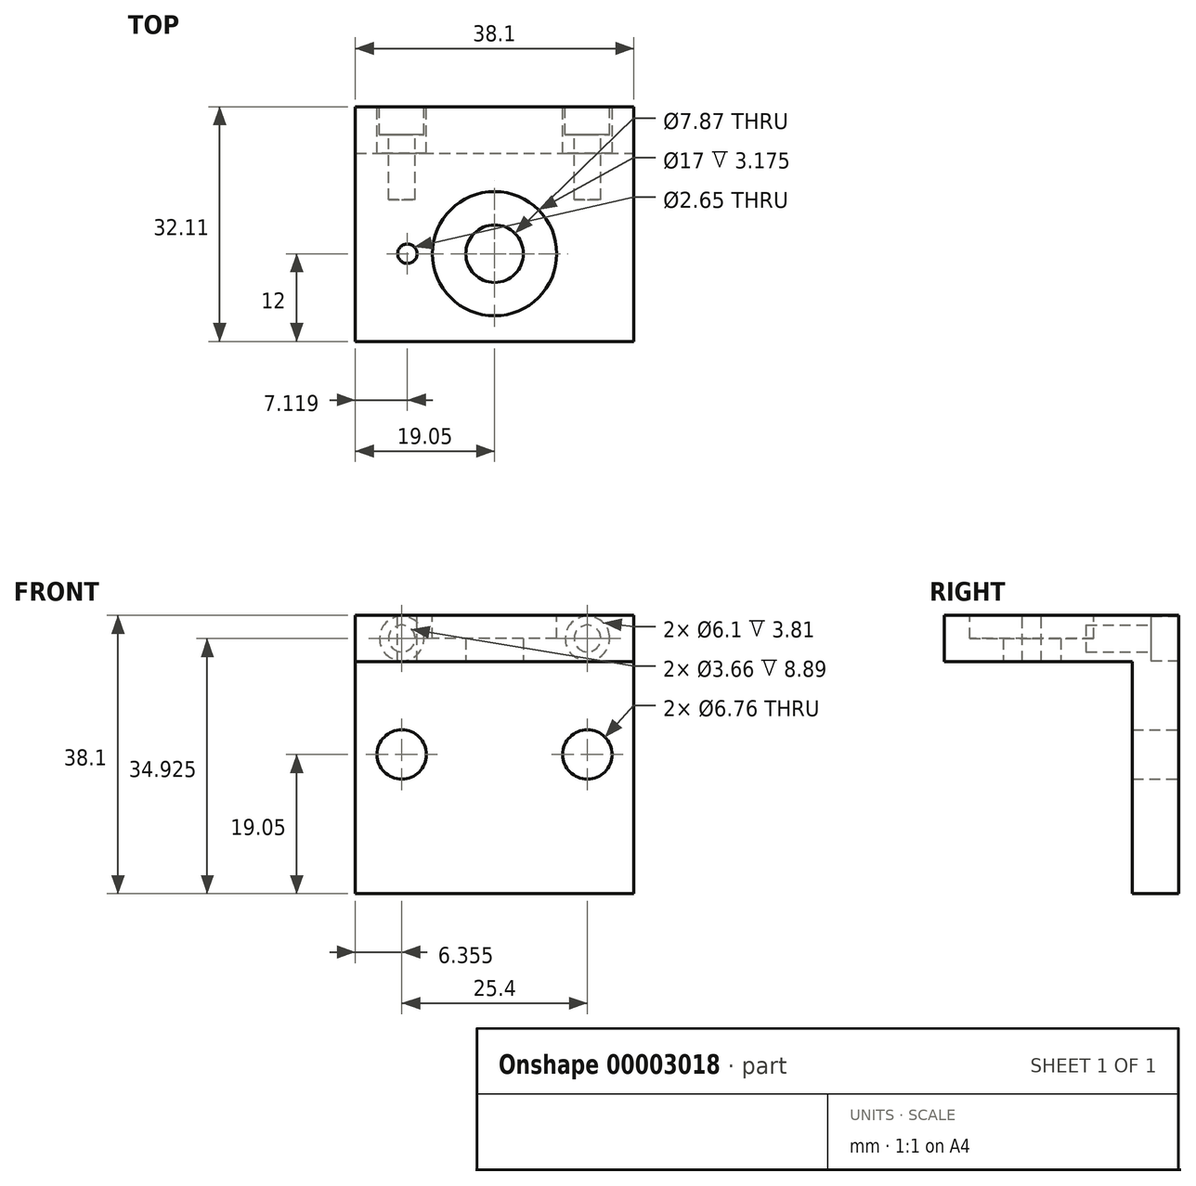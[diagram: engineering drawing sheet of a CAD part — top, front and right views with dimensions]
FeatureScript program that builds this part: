
annotation { "Feature Type Name" : "Feature", "Feature Type Description" : "" }
export const myFeature = defineFeature(function(context is Context, id is Id, definition is map)
    precondition{}
    {
        {
            var Q0;
            Q0=qCreatedBy(makeId("Top.planeOp"),FACE);
            var sketch = newSketch(context, id + "F0", { "sketchPlane" : qUnion([Q0])});
            skCircle(sketch, "E0", {"center": v(0, 0) * mm, "radius": 3.94 * mm});
            skArc(sketch, "E1", {"start": v(-11.93, 1.32) * mm, "mid": v(-12, 0) * mm, "end": v(-11.93, -1.33) * mm});
            skLineSegment(sketch, "E2", {"start": v(-10.8, 0.7) * mm, "end": v(-10.8, -0.7) * mm});
            skLineSegment(sketch, "E3", {"start": v(-11.93, 1.32) * mm, "end": v(-10.8, 0.7) * mm});
            skLineSegment(sketch, "E4.0.MirrorCS", {"start": v(-11.93, -1.32) * mm, "end": v(-10.8, -0.7) * mm});
            skCircle(sketch, "E5", {"center": v(0, 0) * mm, "radius": 12 * mm});
            skSolve(sketch);
        }
        {
            var Q0;
            Q0=makeQuery(id+"F0.imprint","IMPRINT",FACE,{"disambiguationData":[TD([[makeQuery(id+"F0.imprint","IMPRINT",EDGE,{"derivedFrom":sQuery(id+"F0.wireOp",EDGE,"E0")}),-1.0]])]});
            extrude(context, id + "F1", {"entities" : qUnion([Q0]), "depth" : 6.35 * mm});
        }
        {
            var Q0;
            Q0=makeQuery(id+"F1.opExtrude","CAP_FACE",FACE,{"disambiguationData":[OSD([sQuery(id+"F0.wireOp",EDGE,"E0"),sQuery(id+"F0.wireOp",EDGE,"E2"),sQuery(id+"F0.wireOp",EDGE,"E3"),sQuery(id+"F0.wireOp",EDGE,"E4.0.MirrorCS"),sQuery(id+"F0.wireOp",EDGE,"E5")])],"isStart":false});
            var sketch = newSketch(context, id + "F2", { "sketchPlane" : qUnion([Q0])});
            skCircle(sketch, "E6", {"center": v(0, 0) * mm, "radius": 8.5 * mm});
            skSolve(sketch);
        }
        {
            var Q0;
            Q0=makeQuery(id+"F2.imprint","IMPRINT",FACE,{"disambiguationData":[TD([[makeQuery(id+"F2.imprint","IMPRINT",EDGE,{"derivedFrom":sQuery(id+"F2.wireOp",EDGE,"E6")}),1.0]])]});
            extrude(context, id + "F3", {"entities" : qUnion([Q0]), "operationType" : NewBodyOperationType.REMOVE, "oppositeDirection" : true, "depth" : 3.17 * mm});
        }
        {
            var Q0;
            Q0=makeQuery(id+"F1.opExtrude","CAP_FACE",FACE,{"disambiguationData":[OSD([sQuery(id+"F0.wireOp",EDGE,"E0"),sQuery(id+"F0.wireOp",EDGE,"E2"),sQuery(id+"F0.wireOp",EDGE,"E3"),sQuery(id+"F0.wireOp",EDGE,"E4.0.MirrorCS"),sQuery(id+"F0.wireOp",EDGE,"E5")])],"isStart":false});
            var sketch = newSketch(context, id + "F4", { "sketchPlane" : qUnion([Q0])});
            skLineSegment(sketch, "E7.bottom", {"start": v(-11.93, 1.33) * mm, "end": v(11.94, 1.33) * mm});
            skLineSegment(sketch, "E7.top", {"start": v(-11.93, 13.76) * mm, "end": v(11.94, 13.76) * mm});
            skLineSegment(sketch, "E7.left", {"start": v(-11.93, 1.33) * mm, "end": v(-11.93, 13.76) * mm});
            skLineSegment(sketch, "E7.right", {"start": v(11.94, 1.33) * mm, "end": v(11.94, 13.76) * mm});
            skSolve(sketch);
        }
        {
            var Q0;
            Q0=makeQuery(id+"F4.imprint","IMPRINT",FACE,{"disambiguationData":[TD([[makeQuery(id+"F4.imprint","IMPRINT",EDGE,{"derivedFrom":sQuery(id+"F4.wireOp",EDGE,"E7.top")}),-1.0]])]});
            extrude(context, id + "F5", {"entities" : qUnion([Q0]), "operationType" : NewBodyOperationType.ADD, "oppositeDirection" : true, "depth" : 6.35 * mm});
        }
        {
            var Q0;
            Q0=makeQuery(id+"F5.opExtrude","SWEPT_FACE",FACE,{"disambiguationData":[OSD([sQuery(id+"F4.wireOp",EDGE,"E7.top")])]});
            var sketch = newSketch(context, id + "F6", { "sketchPlane" : qUnion([Q0])});
            skLineSegment(sketch, "E8.bottom", {"start": v(-19.05, 6.35) * mm, "end": v(19.05, 6.35) * mm});
            skLineSegment(sketch, "E8.top", {"start": v(-19.05, -31.75) * mm, "end": v(19.05, -31.75) * mm});
            skLineSegment(sketch, "E8.left", {"start": v(-19.05, 6.35) * mm, "end": v(-19.05, -31.75) * mm});
            skLineSegment(sketch, "E8.right", {"start": v(19.05, 6.35) * mm, "end": v(19.05, -31.75) * mm});
            skSolve(sketch);
        }
        {
            var Q0;
            Q0=makeQuery(id+"F6.imprint","IMPRINT",FACE,{"disambiguationData":[TD([[makeQuery(id+"F6.imprint","IMPRINT",EDGE,{"derivedFrom":sQuery(id+"F6.wireOp",EDGE,"E8.top")}),1.0]])]});
            var Q1;
            {var subQ0=sQuery(id+"F4.wireOp",EDGE,"E7.top");Q1=makeQuery(id+"F6.imprint","IMPRINT",FACE,{"disambiguationData":[TD([[makeQuery(id+"F6.imprint","IMPRINT",EDGE,{"derivedFrom":makeQuery(id+"F5.opExtrude","CAP_EDGE",EDGE,{"disambiguationData":[OSD([subQ0])],"isStart":false})}),-1.0]])]});}
            extrude(context, id + "F7", {"entities" : qUnion([Q0, Q1]), "depth" : 6.35 * mm});
        }
        {
            var Q0;
            Q0=makeQuery(id+"F7.opExtrude","SWEPT_FACE",FACE,{"disambiguationData":[OSD([sQuery(id+"F6.wireOp",EDGE,"E8.bottom")])]});
            var sketch = newSketch(context, id + "F8", { "sketchPlane" : qUnion([Q0])});
            skPoint(sketch, "E9", {"position": v(19.05, 13.76) * mm});
            skPoint(sketch, "E10", {"position": v(-19.05, 13.76) * mm});
            skLineSegment(sketch, "E11.0.0", {"start": v(-11.93, 1.33) * mm, "end": v(-10.8, 0.7) * mm});
            skLineSegment(sketch, "E11.0.1", {"start": v(-10.8, 0.7) * mm, "end": v(-10.8, -0.7) * mm});
            skLineSegment(sketch, "E11.0.2", {"start": v(-11.93, -1.33) * mm, "end": v(-10.8, -0.7) * mm});
            skArc(sketch, "E11.0.3", {"start": v(-11.93, -1.32) * mm, "mid": v(1.32, -11.93) * mm, "end": v(11.93, 1.32) * mm});
            skLineSegment(sketch, "E11.0.4", {"start": v(11.93, 1.33) * mm, "end": v(11.94, 1.33) * mm});
            skLineSegment(sketch, "E11.0.5", {"start": v(11.94, 1.33) * mm, "end": v(11.94, 13.76) * mm});
            skLineSegment(sketch, "E11.0.6", {"start": v(-11.93, 13.76) * mm, "end": v(11.94, 13.76) * mm});
            skLineSegment(sketch, "E11.0.7", {"start": v(-11.93, 1.33) * mm, "end": v(-11.93, 13.76) * mm});
            skPoint(sketch, "E12", {"position": v(0, -12) * mm});
            skLineSegment(sketch, "E13.bottom", {"start": v(-19.05, 13.76) * mm, "end": v(19.05, 13.76) * mm});
            skLineSegment(sketch, "E13.top", {"start": v(-19.05, -12) * mm, "end": v(19.05, -12) * mm});
            skLineSegment(sketch, "E13.left", {"start": v(-19.05, 13.76) * mm, "end": v(-19.05, -12) * mm});
            skLineSegment(sketch, "E13.right", {"start": v(19.05, 13.76) * mm, "end": v(19.05, -12) * mm});
            skCircle(sketch, "E14", {"center": v(-11.93, 0) * mm, "radius": 1.33 * mm});
            skSolve(sketch);
        }
        {
            var Q0;
            {var subQ3=sQuery(id+"F8.wireOp",EDGE,"E11.0.7");Q0=makeQuery(id+"F8.imprint","IMPRINT",FACE,{"disambiguationData":[TD([[makeQuery(id+"F8.imprint","IMPRINT",EDGE,{"derivedFrom":subQ3}),1.0]])]});}
            var Q1;
            {var subQ6=sQuery(id+"F8.wireOp",EDGE,"E11.0.4");Q1=makeQuery(id+"F8.imprint","IMPRINT",FACE,{"disambiguationData":[TD([[makeQuery(id+"F8.imprint","IMPRINT",EDGE,{"derivedFrom":subQ6}),-1.0]])]});}
            extrude(context, id + "F9", {"entities" : qUnion([Q0, Q1]), "operationType" : NewBodyOperationType.ADD, "oppositeDirection" : true, "depth" : 6.35 * mm});
        }
        {
            var Q0;
            {var subQ1=sQuery(id+"F8.wireOp",EDGE,"E11.0.2");Q0=makeQuery(id+"F8.imprint","IMPRINT",FACE,{"disambiguationData":[TD([[makeQuery(id+"F8.imprint","IMPRINT",EDGE,{"derivedFrom":subQ1}),-1.0]])]});}
            var Q1;
            {var subQ1=sQuery(id+"F8.wireOp",EDGE,"E11.0.1");Q1=makeQuery(id+"F8.imprint","IMPRINT",FACE,{"disambiguationData":[TD([[makeQuery(id+"F8.imprint","IMPRINT",EDGE,{"derivedFrom":subQ1}),1.0]])]});}
            var Q2;
            {var subQ1=sQuery(id+"F8.wireOp",EDGE,"E11.0.0");Q2=makeQuery(id+"F8.imprint","IMPRINT",FACE,{"disambiguationData":[TD([[makeQuery(id+"F8.imprint","IMPRINT",EDGE,{"derivedFrom":subQ1}),1.0]])]});}
            extrude(context, id + "F10", {"entities" : qUnion([Q0, Q1, Q2]), "operationType" : NewBodyOperationType.REMOVE, "oppositeDirection" : true, "depth" : 25.4 * mm});
        }
        {
            var Q0;
            Q0=makeQuery(id+"F7.opExtrude","CAP_FACE",FACE,{"disambiguationData":[OSD([sQuery(id+"F6.wireOp",EDGE,"E8.bottom"),sQuery(id+"F6.wireOp",EDGE,"E8.top"),sQuery(id+"F6.wireOp",EDGE,"E8.left"),sQuery(id+"F6.wireOp",EDGE,"E8.right")])],"isStart":false});
            var sketch = newSketch(context, id + "F11", { "sketchPlane" : qUnion([Q0])});
            skCircle(sketch, "E15", {"center": v(-12.7, 3.18) * mm, "radius": 1.83 * mm});
            skPoint(sketch, "E15.first.point", {"position": v(-14.53, 3.01) * mm});
            skPoint(sketch, "E15.second.point", {"position": v(-11.71, 1.64) * mm});
            skPoint(sketch, "E15.third.point", {"position": v(-10.88, 3.2) * mm});
            skCircle(sketch, "E16", {"center": v(12.7, 3.18) * mm, "radius": 1.83 * mm});
            skSolve(sketch);
        }
        {
            var Q0;
            Q0=makeQuery(id+"F11.imprint","IMPRINT",FACE,{"disambiguationData":[TD([[makeQuery(id+"F11.imprint","IMPRINT",EDGE,{"derivedFrom":sQuery(id+"F11.wireOp",EDGE,"E15")}),1.0]])]});
            var Q1;
            Q1=makeQuery(id+"F11.imprint","IMPRINT",FACE,{"disambiguationData":[TD([[makeQuery(id+"F11.imprint","IMPRINT",EDGE,{"derivedFrom":sQuery(id+"F11.wireOp",EDGE,"E16")}),1.0]])]});
            extrude(context, id + "F12", {"entities" : qUnion([Q0, Q1]), "operationType" : NewBodyOperationType.REMOVE, "oppositeDirection" : true, "depth" : 12.7 * mm});
        }
        {
            var Q0;
            Q0=makeQuery(id+"F7.opExtrude","CAP_FACE",FACE,{"disambiguationData":[OSD([sQuery(id+"F6.wireOp",EDGE,"E8.bottom"),sQuery(id+"F6.wireOp",EDGE,"E8.top"),sQuery(id+"F6.wireOp",EDGE,"E8.left"),sQuery(id+"F6.wireOp",EDGE,"E8.right")])],"isStart":false});
            var sketch = newSketch(context, id + "F13", { "sketchPlane" : qUnion([Q0])});
            skCircle(sketch, "E17", {"center": v(-12.7, 3.18) * mm, "radius": 3.05 * mm});
            skCircle(sketch, "E18", {"center": v(12.7, 3.18) * mm, "radius": 3.05 * mm});
            skSolve(sketch);
        }
        {
            var Q0;
            Q0=makeQuery(id+"F13.imprint","IMPRINT",FACE,{"disambiguationData":[TD([[makeQuery(id+"F13.imprint","IMPRINT",EDGE,{"derivedFrom":sQuery(id+"F13.wireOp",EDGE,"E17")}),1.0]])]});
            var Q1;
            Q1=makeQuery(id+"F13.imprint","IMPRINT",FACE,{"disambiguationData":[TD([[makeQuery(id+"F13.imprint","IMPRINT",EDGE,{"derivedFrom":sQuery(id+"F13.wireOp",EDGE,"E18")}),1.0]])]});
            extrude(context, id + "F14", {"entities" : qUnion([Q0, Q1]), "operationType" : NewBodyOperationType.REMOVE, "oppositeDirection" : true, "depth" : 3.8 * mm});
        }
        {
            var Q0;
            Q0=makeQuery(id+"F7.opExtrude","CAP_FACE",FACE,{"disambiguationData":[OSD([sQuery(id+"F6.wireOp",EDGE,"E8.bottom"),sQuery(id+"F6.wireOp",EDGE,"E8.top"),sQuery(id+"F6.wireOp",EDGE,"E8.left"),sQuery(id+"F6.wireOp",EDGE,"E8.right")])],"isStart":false});
            var sketch = newSketch(context, id + "F15", { "sketchPlane" : qUnion([Q0])});
            skCircle(sketch, "E19", {"center": v(-12.7, -12.7) * mm, "radius": 3.38 * mm});
            skCircle(sketch, "E20", {"center": v(12.7, -12.7) * mm, "radius": 3.38 * mm});
            skSolve(sketch);
        }
        {
            var Q0;
            Q0=makeQuery(id+"F15.imprint","IMPRINT",FACE,{"disambiguationData":[TD([[makeQuery(id+"F15.imprint","IMPRINT",EDGE,{"derivedFrom":sQuery(id+"F15.wireOp",EDGE,"E20")}),1.0]])]});
            var Q1;
            Q1=makeQuery(id+"F15.imprint","IMPRINT",FACE,{"disambiguationData":[TD([[makeQuery(id+"F15.imprint","IMPRINT",EDGE,{"derivedFrom":sQuery(id+"F15.wireOp",EDGE,"E19")}),1.0]])]});
            extrude(context, id + "F16", {"entities" : qUnion([Q0, Q1]), "operationType" : NewBodyOperationType.REMOVE, "oppositeDirection" : true, "depth" : 25.4 * mm});
        }
    });
